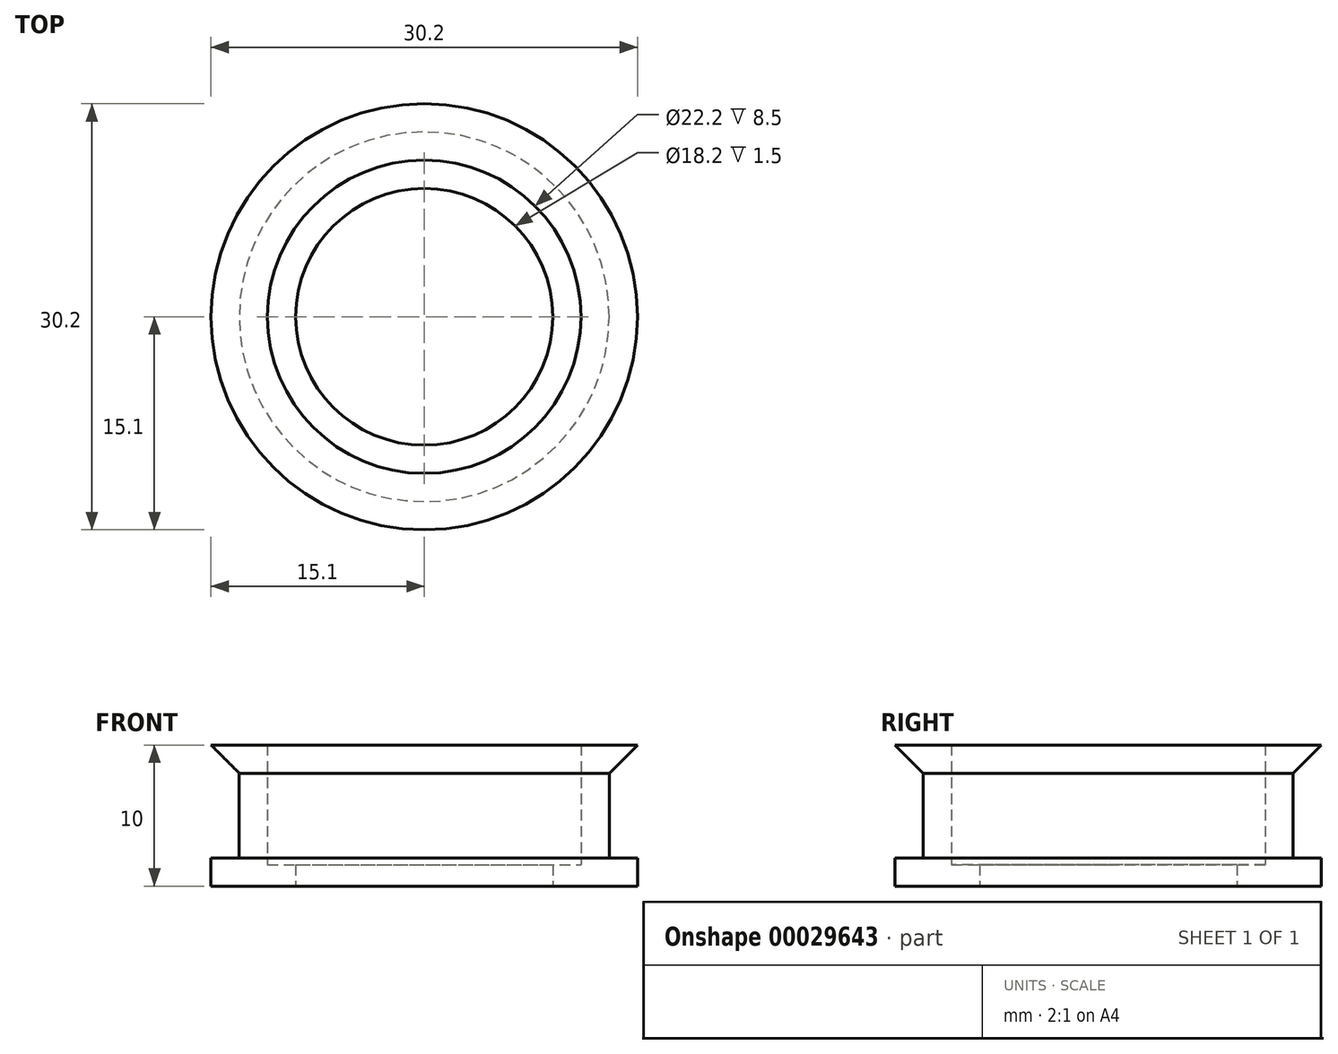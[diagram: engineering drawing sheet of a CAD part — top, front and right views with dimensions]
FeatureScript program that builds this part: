
annotation { "Feature Type Name" : "Feature", "Feature Type Description" : "" }
export const myFeature = defineFeature(function(context is Context, id is Id, definition is map)
    precondition{}
    {
        {
            var Q0;
            Q0=qCreatedBy(makeId("Front.planeOp"),FACE);
            var sketch = newSketch(context, id + "F0", { "sketchPlane" : qUnion([Q0])});
            skLineSegment(sketch, "E0", {"start": v(11.1, 4.8) * mm, "end": v(15.1, 4.8) * mm});
            skLineSegment(sketch, "E1", {"start": v(15.1, 4.8) * mm, "end": v(13.1, 2.8) * mm});
            skLineSegment(sketch, "E2", {"start": v(13.1, 2.8) * mm, "end": v(13.1, -3.2) * mm});
            skLineSegment(sketch, "E3", {"start": v(13.1, -3.2) * mm, "end": v(15.1, -5.2) * mm, "construction": true});
            skLineSegment(sketch, "E4", {"start": v(15.1, -5.2) * mm, "end": v(11.1, -5.2) * mm});
            skLineSegment(sketch, "E5", {"start": v(11.1, -5.2) * mm, "end": v(11.1, 4.8) * mm});
            skLineSegment(sketch, "E6", {"start": v(0, -3.77) * mm, "end": v(0, 4.95) * mm, "construction": true});
            skLineSegment(sketch, "E7.bottom", {"start": v(11.1, -5.2) * mm, "end": v(9.1, -5.2) * mm});
            skLineSegment(sketch, "E7.top", {"start": v(11.1, -3.7) * mm, "end": v(9.1, -3.7) * mm});
            skLineSegment(sketch, "E7.left", {"start": v(11.1, -5.2) * mm, "end": v(11.1, -3.7) * mm});
            skLineSegment(sketch, "E7.right", {"start": v(9.1, -5.2) * mm, "end": v(9.1, -3.7) * mm});
            skLineSegment(sketch, "E8", {"start": v(13.1, -3.2) * mm, "end": v(15.1, -3.2) * mm});
            skLineSegment(sketch, "E9", {"start": v(15.1, -3.2) * mm, "end": v(15.1, -5.2) * mm});
            skSolve(sketch);
        }
        {
            var Q0;
            Q0=qSketchRegion(id+"F0",true);
            var Q1;
            Q1=sQuery(id+"F0.wireOp",EDGE,"E6");
            revolve(context, id + "F1", {"entities" : qUnion([Q0]), "axis" : qUnion([Q1]), "revolveType" : RevolveType.FULL});
        }
    });
